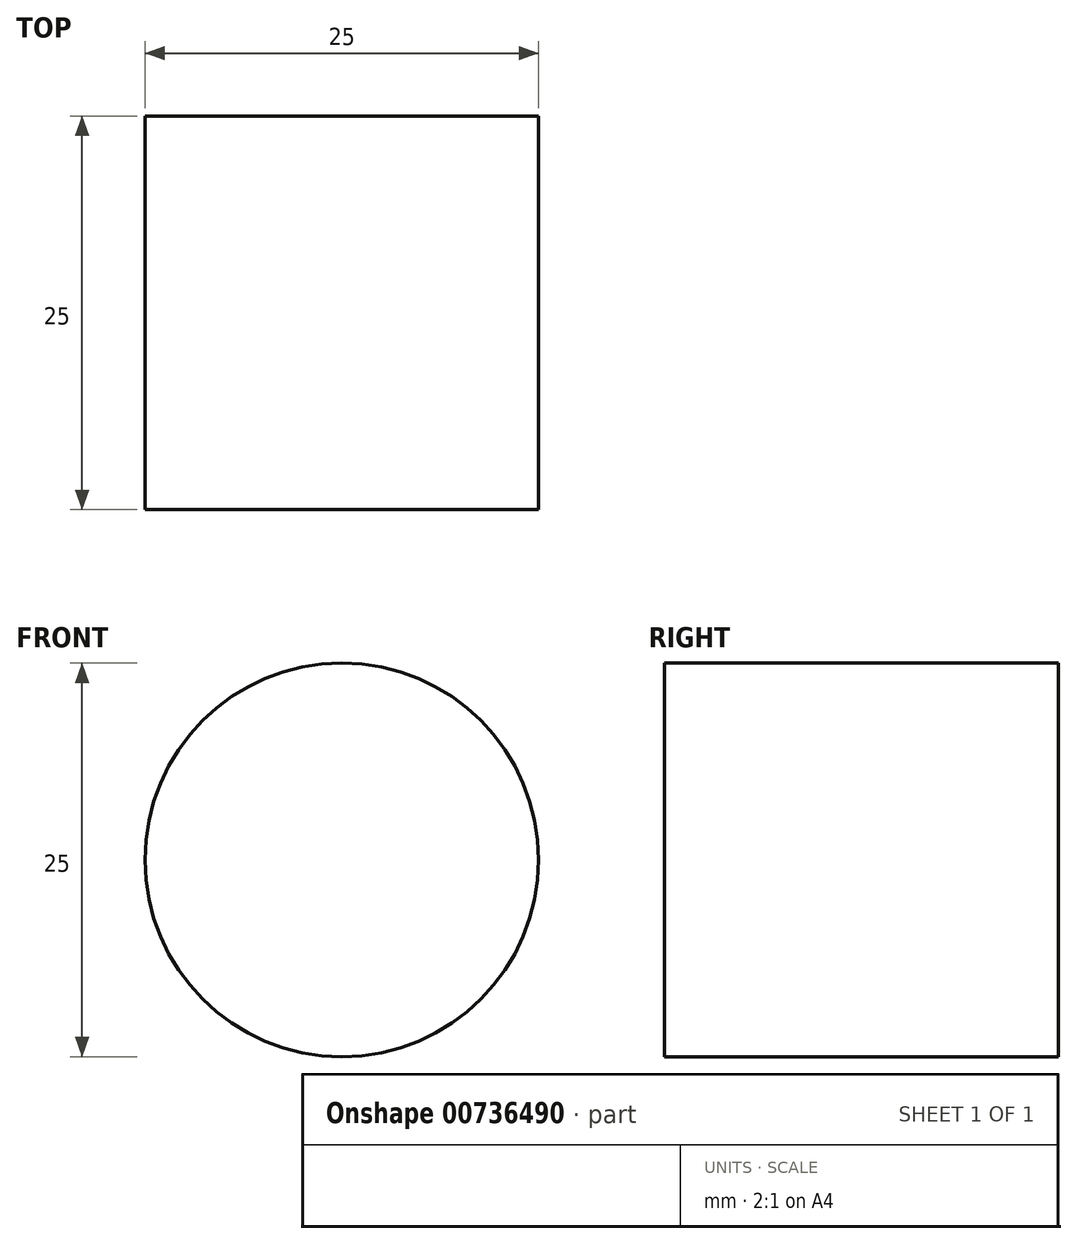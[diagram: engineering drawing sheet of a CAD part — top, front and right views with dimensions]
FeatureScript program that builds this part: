
annotation { "Feature Type Name" : "Feature", "Feature Type Description" : "" }
export const myFeature = defineFeature(function(context is Context, id is Id, definition is map)
    precondition{}
    {
        {
            var Q0;
            Q0=qCreatedBy(makeId("Front.planeOp"),FACE);
            var sketch = newSketch(context, id + "F0", { "sketchPlane" : qUnion([Q0])});
            skCircle(sketch, "E0", {"center": v(0, 0) * mm, "radius": 12.5 * mm});
            skCircle(sketch, "E1", {"center": v(0, 40) * mm, "radius": 10 * mm});
            skSolve(sketch);
        }
        {
            var Q0;
            Q0=makeQuery(id+"F0.imprint","IMPRINT",FACE,{"disambiguationData":[TD([[makeQuery(id+"F0.imprint","IMPRINT",EDGE,{"derivedFrom":sQuery(id+"F0.wireOp",EDGE,"E0")}),1.0]])]});
            var Q1;
            Q1=makeQuery(id+"F0.imprint","IMPRINT",FACE,{"disambiguationData":[TD([[makeQuery(id+"F0.imprint","IMPRINT",EDGE,{"derivedFrom":sQuery(id+"F0.wireOp",EDGE,"E1")}),1.0]])]});
            extrude(context, id + "F1", {"entities" : qUnion([Q0, Q1]), "depth" : 25 * mm, "offsetDistance" : 25 * mm});
        }
        {
            var Q0;
            Q0=makeQuery(id+"F1.opExtrude","SWEPT_BODY",BODY,{"disambiguationData":[OSD([sQuery(id+"F0.wireOp",EDGE,"E1")])]});
            deleteBodies(context, id + "F2", {"entities" : qUnion([Q0])});
        }
    });
